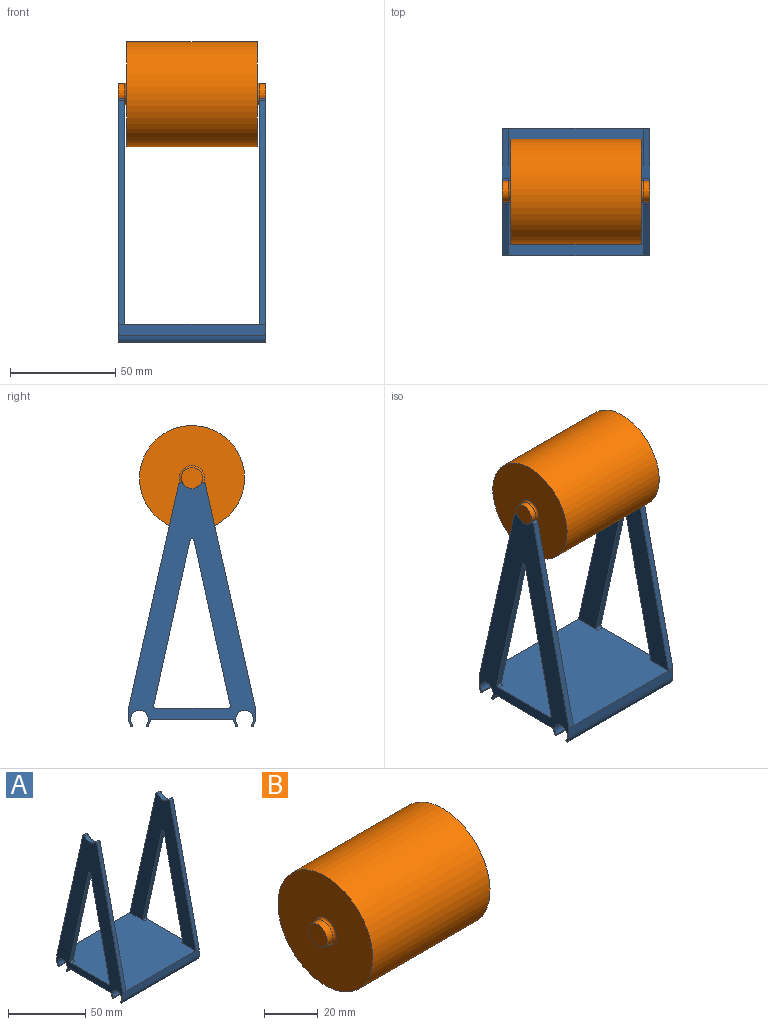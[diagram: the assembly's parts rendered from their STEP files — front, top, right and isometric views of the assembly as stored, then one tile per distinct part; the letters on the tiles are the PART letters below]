
ASSEMBLY  parts=2 mates=1
PART A: 42 faces, bbox 70x60.5x116.1 mm
  f0: plane 70x60.5mm, normal (0,0,1), area 4078.8mm2, adj f5,f6,f16,f17,f23,f29,f32,f34
  f1: cylinder r=0.5mm len=70mm, axis (-1,0,0), area 110mm2, adj f2,f15,f16,f17
  f2: cylinder r=4.25mm len=70mm, axis (-1,0,0), area 1327.8mm2, adj f1,f3,f16,f17
  f3: cylinder r=0.5mm len=70mm, axis (-1,0,0), area 110mm2, adj f2,f4,f16,f17
  f4: cylinder r=5.25mm len=70mm, axis (-1,0,0), area 242.9mm2, adj f3,f5,f16,f17
  f5: plane 70x5.25mm, normal (0,1,0), area 367.5mm2, adj f0,f4,f16,f17,f21,f27
  f6: plane 70x5.25mm, normal (0,-1,0), area 367.5mm2, adj f0,f7,f16,f17,f18,f24
  f7: cylinder r=5.25mm len=70mm, axis (-1,0,0), area 242.9mm2, adj f6,f8,f16,f17
  f8: cylinder r=0.5mm len=70mm, axis (-1,0,0), area 110mm2, adj f7,f9,f16,f17
  f9: cylinder r=4.25mm len=70mm, axis (-1,0,0), area 1327.8mm2, adj f8,f10,f16,f17
  f10: cylinder r=0.5mm len=70mm, axis (-1,0,0), area 110mm2, adj f9,f11,f16,f17
  f11: cylinder r=5.25mm len=70mm, axis (-1,0,0), area 163.6mm2, adj f10,f12,f16,f17
  f12: plane 70x0.34mm, normal (0,0.98,-0.21), area 24.2mm2, adj f11,f16,f17,f41
  f13: plane 70x37.64mm, normal (0,0,-1), area 2634.9mm2, adj f16,f17,f40,f41
  f14: plane 70x0.34mm, normal (0,-0.98,-0.21), area 24.2mm2, adj f15,f16,f17,f40
  f15: cylinder r=5.25mm len=70mm, axis (-1,0,0), area 163.6mm2, adj f1,f14,f16,f17
  f16: plane 116.07x60.5mm, normal (1,0,0), area 2618mm2, adj f0,f1,f2,f3,f4,f5,f6,f7
  f17: plane 116.07x60.5mm, normal (-1,0,0), area 2618mm2, adj f0,f1,f2,f3,f4,f5,f6,f7
  f18: plane 106.62x23.86mm, normal (0,-0.98,0.22), area 327.8mm2, adj f6,f17,f23,f35
  f19: plane 78.63x17.23mm, normal (0,0.98,-0.21), area 241.5mm2, adj f17,f23,f37,f38
  f20: plane 78.63x17.23mm, normal (0,-0.98,-0.21), area 241.5mm2, adj f17,f23,f38,f39
  f21: plane 106.62x23.86mm, normal (0,0.98,0.22), area 327.8mm2, adj f5,f17,f23,f36
  f22: cylinder r=5.5mm len=9.17mm, axis (-1,0,0), area 32.5mm2, adj f17,f23,f35,f36
  f23: plane 107.41x60.5mm, normal (1,0,0), area 2342.6mm2, adj f0,f18,f19,f20,f21,f22,f35,f36
  f24: plane 106.62x23.86mm, normal (0,-0.98,0.22), area 327.8mm2, adj f6,f16,f29,f30
  f25: plane 78.63x17.23mm, normal (0,0.98,-0.21), area 241.5mm2, adj f16,f29,f32,f33
  f26: plane 78.63x17.23mm, normal (0,-0.98,-0.21), area 241.5mm2, adj f16,f29,f33,f34
  f27: plane 106.62x23.86mm, normal (0,0.98,0.22), area 327.8mm2, adj f5,f16,f29,f31
  f28: cylinder r=5.5mm len=9.17mm, axis (-1,0,0), area 32.5mm2, adj f16,f29,f30,f31
  f29: plane 107.41x60.5mm, normal (-1,0,0), area 2342.6mm2, adj f0,f24,f25,f26,f27,f28,f30,f31
  f30: cylinder r=1mm len=3mm, axis (-1,0,0), area 7mm2, adj f16,f24,f28,f29
  f31: cylinder r=1mm len=3mm, axis (-1,0,0), area 7mm2, adj f16,f27,f28,f29
  f32: cylinder r=1mm len=3mm, axis (-1,0,0), area 5.4mm2, adj f0,f16,f25,f29
  f33: cylinder r=1mm len=3mm, axis (-1,0,0), area 8.1mm2, adj f16,f25,f26,f29
  f34: cylinder r=1mm len=3mm, axis (1,0,0), area 5.4mm2, adj f0,f16,f26,f29
  f35: cylinder r=1mm len=3mm, axis (-1,0,0), area 7mm2, adj f17,f18,f22,f23
  f36: cylinder r=1mm len=3mm, axis (-1,0,0), area 7mm2, adj f17,f21,f22,f23
  f37: cylinder r=1mm len=3mm, axis (-1,0,0), area 5.4mm2, adj f0,f17,f19,f23
  f38: cylinder r=1mm len=3mm, axis (-1,0,0), area 8.1mm2, adj f17,f19,f20,f23
  f39: cylinder r=1mm len=3mm, axis (1,0,0), area 5.4mm2, adj f0,f17,f20,f23
  f40: cylinder r=1mm len=70mm, axis (-1,0,0), area 94.9mm2, adj f13,f14,f16,f17
  f41: cylinder r=1mm len=70mm, axis (1,0,0), area 94.9mm2, adj f12,f13,f16,f17
PART B: 9 faces, bbox 70x50x50 mm
  f0: cylinder r=5mm len=10mm, axis (-1,0,0), area 94.2mm2, adj f1,f8
  f1: plane 10x10mm, normal (1,0,0), area 78.5mm2, adj f0
  f2: cylinder r=25mm len=62mm, axis (-1,0,0), area 9738.9mm2, adj f3,f4
  f3: plane 50x50mm, normal (1,0,0), area 1850.4mm2, adj f2,f8
  f4: plane 50x50mm, normal (-1,0,0), area 1850.4mm2, adj f2,f7
  f5: plane 10x10mm, normal (-1,0,0), area 78.5mm2, adj f6
  f6: cylinder r=5mm len=10mm, axis (-1,0,0), area 94.2mm2, adj f5,f7
  f7: torus R=6mm, axis (1,0,0), area 52.9mm2, adj f4,f6
  f8: torus R=6mm, axis (1,0,0), area 52.9mm2, adj f0,f3
PLACE A t=(-34.98,27.76,34.53)mm fixed
PLACE B rot(axis=(0,0.99,-0.15),180deg) t=(35.02,27.76,34.03)mm
MATE planar B.f0 <-> A.f16  axis (1,0,0) through (35.02,27.76,34.03)mm
